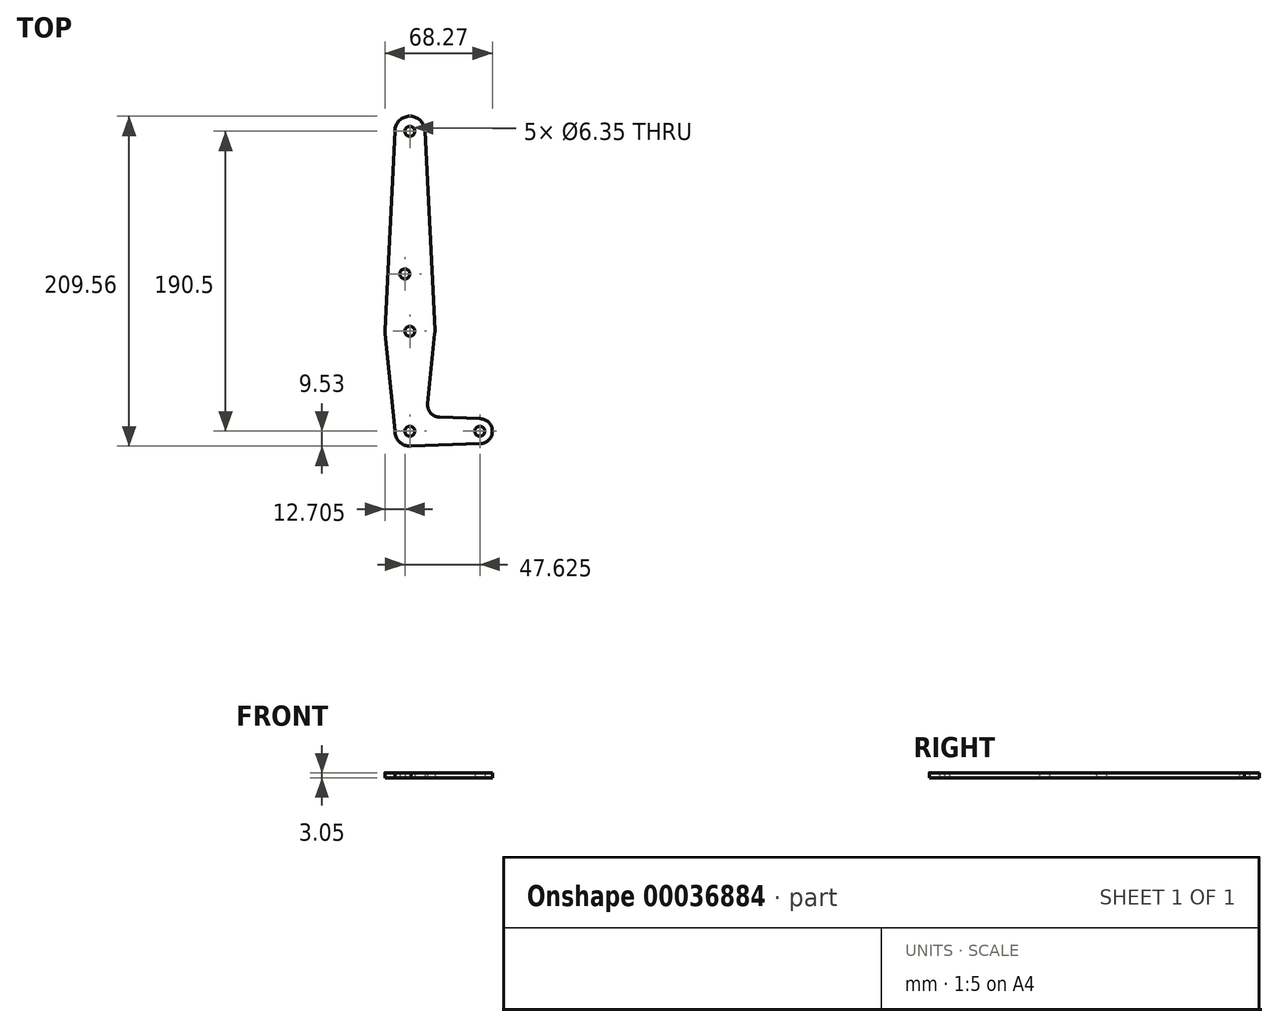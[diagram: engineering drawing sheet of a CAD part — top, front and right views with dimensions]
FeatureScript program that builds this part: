
annotation { "Feature Type Name" : "Feature", "Feature Type Description" : "" }
export const myFeature = defineFeature(function(context is Context, id is Id, definition is map)
    precondition{}
    {
        {
            var Q0;
            Q0=qCreatedBy(makeId("Top.planeOp"),FACE);
            var sketch = newSketch(context, id + "F0", { "sketchPlane" : qUnion([Q0])});
            skLineSegment(sketch, "E0", {"start": v(0, 0) * mm, "end": v(0, 190.5) * mm, "construction": true});
            skLineSegment(sketch, "E1", {"start": v(0, 0) * mm, "end": v(44.45, 0) * mm, "construction": true});
            skCircle(sketch, "E2", {"center": v(0, 190.5) * mm, "radius": 9.53 * mm});
            skCircle(sketch, "E3", {"center": v(0, 0) * mm, "radius": 9.53 * mm});
            skCircle(sketch, "E4", {"center": v(44.45, 0) * mm, "radius": 7.94 * mm});
            skCircle(sketch, "E5", {"center": v(0, 63.5) * mm, "radius": 15.88 * mm});
            skLineSegment(sketch, "E6", {"start": v(0, -9.53) * mm, "end": v(44.73, -7.93) * mm});
            skLineSegment(sketch, "E7", {"start": v(18.93, 8.85) * mm, "end": v(44.73, 7.93) * mm});
            skLineSegment(sketch, "E8", {"start": v(-9.53, 0) * mm, "end": v(-15.8, 61.9) * mm});
            skLineSegment(sketch, "E9", {"start": v(-9.52, 190.5) * mm, "end": v(-15.86, 64.3) * mm});
            skLineSegment(sketch, "E10", {"start": v(11.3, 17.6) * mm, "end": v(15.8, 61.9) * mm});
            skLineSegment(sketch, "E11", {"start": v(15.86, 64.3) * mm, "end": v(9.53, 190.5) * mm});
            skCircle(sketch, "E12", {"center": v(0, 190.5) * mm, "radius": 3.18 * mm});
            skCircle(sketch, "E13", {"center": v(0, 0) * mm, "radius": 3.18 * mm});
            skCircle(sketch, "E14", {"center": v(44.45, 0) * mm, "radius": 3.18 * mm});
            skCircle(sketch, "E15", {"center": v(0, 63.5) * mm, "radius": 3.18 * mm});
            skCircle(sketch, "E16", {"center": v(-3.18, 99.89) * mm, "radius": 3.18 * mm});
            skArc(sketch, "E17.filletArc", {"start": v(11.3, 17.6) * mm, "mid": v(13.22, 11.57) * mm, "end": v(18.93, 8.85) * mm});
            skSolve(sketch);
        }
        {
            var Q0;
            Q0 = qSketchRegion(id + "F0", true);
            extrude(context, id + "F1", {"entities" : qUnion([Q0]), "depth" : 3.05 * mm});
        }
    });
